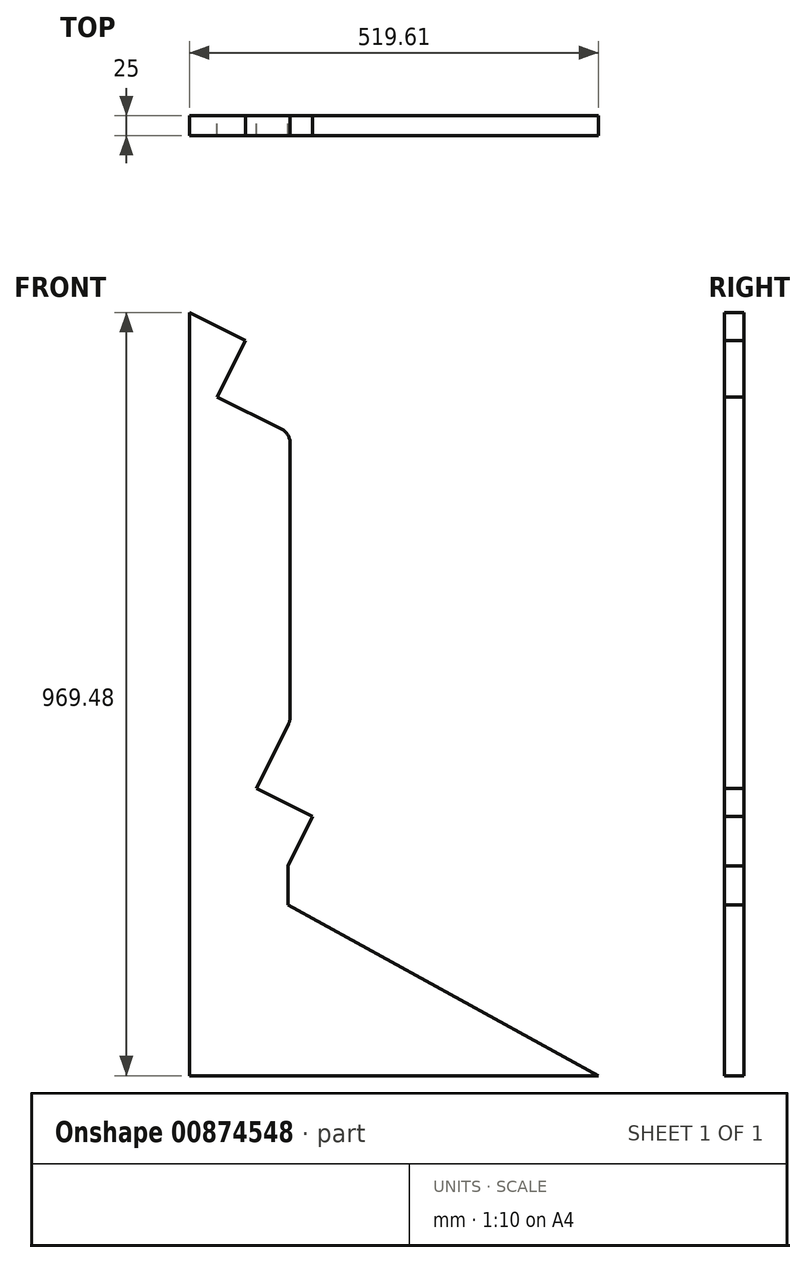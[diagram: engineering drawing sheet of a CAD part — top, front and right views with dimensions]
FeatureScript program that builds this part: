
annotation { "Feature Type Name" : "Feature", "Feature Type Description" : "" }
export const myFeature = defineFeature(function(context is Context, id is Id, definition is map)
    precondition{}
    {
        {
            var Q0;
            Q0=qCreatedBy(makeId("Front.planeOp"),FACE);
            var sketch = newSketch(context, id + "F0", { "sketchPlane" : qUnion([Q0])});
            skLineSegment(sketch, "E0", {"start": v(343.03, -536.9) * mm, "end": v(-51.4, -320.29) * mm});
            skLineSegment(sketch, "E1", {"start": v(-51.4, -320.29) * mm, "end": v(-51.4, -270.29) * mm});
            skLineSegment(sketch, "E2", {"start": v(-51.4, -270.29) * mm, "end": v(-20.04, -207.7) * mm});
            skLineSegment(sketch, "E3", {"start": v(31.49, -81.24) * mm, "end": v(31.49, 266.52) * mm, "construction": true});
            skLineSegment(sketch, "E4", {"start": v(-23.69, 355.91) * mm, "end": v(-60.59, 374.41) * mm, "construction": true});
            skPoint(sketch, "E5.visualSharp", {"position": v(31.49, 328.25) * mm});
            skArc(sketch, "E5.filletArc", {"start": v(31.49, 266.52) * mm, "mid": v(16.58, 319.05) * mm, "end": v(-23.69, 355.91) * mm, "construction": true});
            skPoint(sketch, "E6.visualSharp", {"position": v(31.49, -104.9) * mm});
            skArc(sketch, "E6.filletArc", {"start": v(20.89, -126.05) * mm, "mid": v(28.8, -104.26) * mm, "end": v(31.49, -81.24) * mm, "construction": true});
            skLineSegment(sketch, "E7", {"start": v(-214.08, 433.58) * mm, "end": v(-214.08, -536.9) * mm, "construction": true});
            skLineSegment(sketch, "E8", {"start": v(-176.58, -536.9) * mm, "end": v(343.03, -536.9) * mm});
            skLineSegment(sketch, "E9.0", {"start": v(-37.14, 329.1) * mm, "end": v(-74.03, 347.6) * mm, "construction": true});
            skLineSegment(sketch, "E9.1", {"start": v(-24.46, -149.56) * mm, "end": v(-5.93, -112.6) * mm, "construction": true});
            skArc(sketch, "E9.2", {"start": v(-5.93, -112.6) * mm, "mid": v(-0.4, -97.35) * mm, "end": v(1.49, -81.24) * mm, "construction": true});
            skLineSegment(sketch, "E9.3", {"start": v(1.49, -81.24) * mm, "end": v(1.49, 266.52) * mm, "construction": true});
            skArc(sketch, "E9.4", {"start": v(1.49, 266.52) * mm, "mid": v(-8.95, 303.29) * mm, "end": v(-37.14, 329.1) * mm, "construction": true});
            skLineSegment(sketch, "E10", {"start": v(-60.59, 374.41) * mm, "end": v(-74.03, 347.6) * mm, "construction": true});
            skLineSegment(sketch, "E11.0", {"start": v(-20.04, -207.7) * mm, "end": v(-91.56, -171.86) * mm});
            skLineSegment(sketch, "E11.1", {"start": v(-91.56, -171.86) * mm, "end": v(-50.63, -90.2) * mm});
            skArc(sketch, "E11.2", {"start": v(-50.63, -90.2) * mm, "mid": v(-49.05, -85.84) * mm, "end": v(-48.51, -81.24) * mm});
            skLineSegment(sketch, "E11.3", {"start": v(-105.28, 396.82) * mm, "end": v(-141.14, 325.31) * mm});
            skLineSegment(sketch, "E11.4", {"start": v(-59.55, 284.4) * mm, "end": v(-141.14, 325.31) * mm});
            skArc(sketch, "E11.5", {"start": v(-48.51, 266.52) * mm, "mid": v(-51.5, 277.03) * mm, "end": v(-59.55, 284.4) * mm});
            skLineSegment(sketch, "E11.6", {"start": v(-48.51, -81.24) * mm, "end": v(-48.51, 266.52) * mm});
            skLineSegment(sketch, "E12.trimOffspring", {"start": v(-105.28, 396.82) * mm, "end": v(-178.58, 433.58) * mm});
            skLineSegment(sketch, "E13.trimOffspring", {"start": v(2.36, -163) * mm, "end": v(20.89, -126.05) * mm, "construction": true});
            skLineSegment(sketch, "E14.0", {"start": v(-176.58, 433.58) * mm, "end": v(-176.58, -536.9) * mm});
            skSolve(sketch);
        }
        {
            var Q0;
            Q0 = qSketchRegion(id + "F0", true);
            extrude(context, id + "F1", {"entities" : qUnion([Q0]), "depth" : 25 * mm, "offsetDistance" : 25 * mm});
        }
    });
